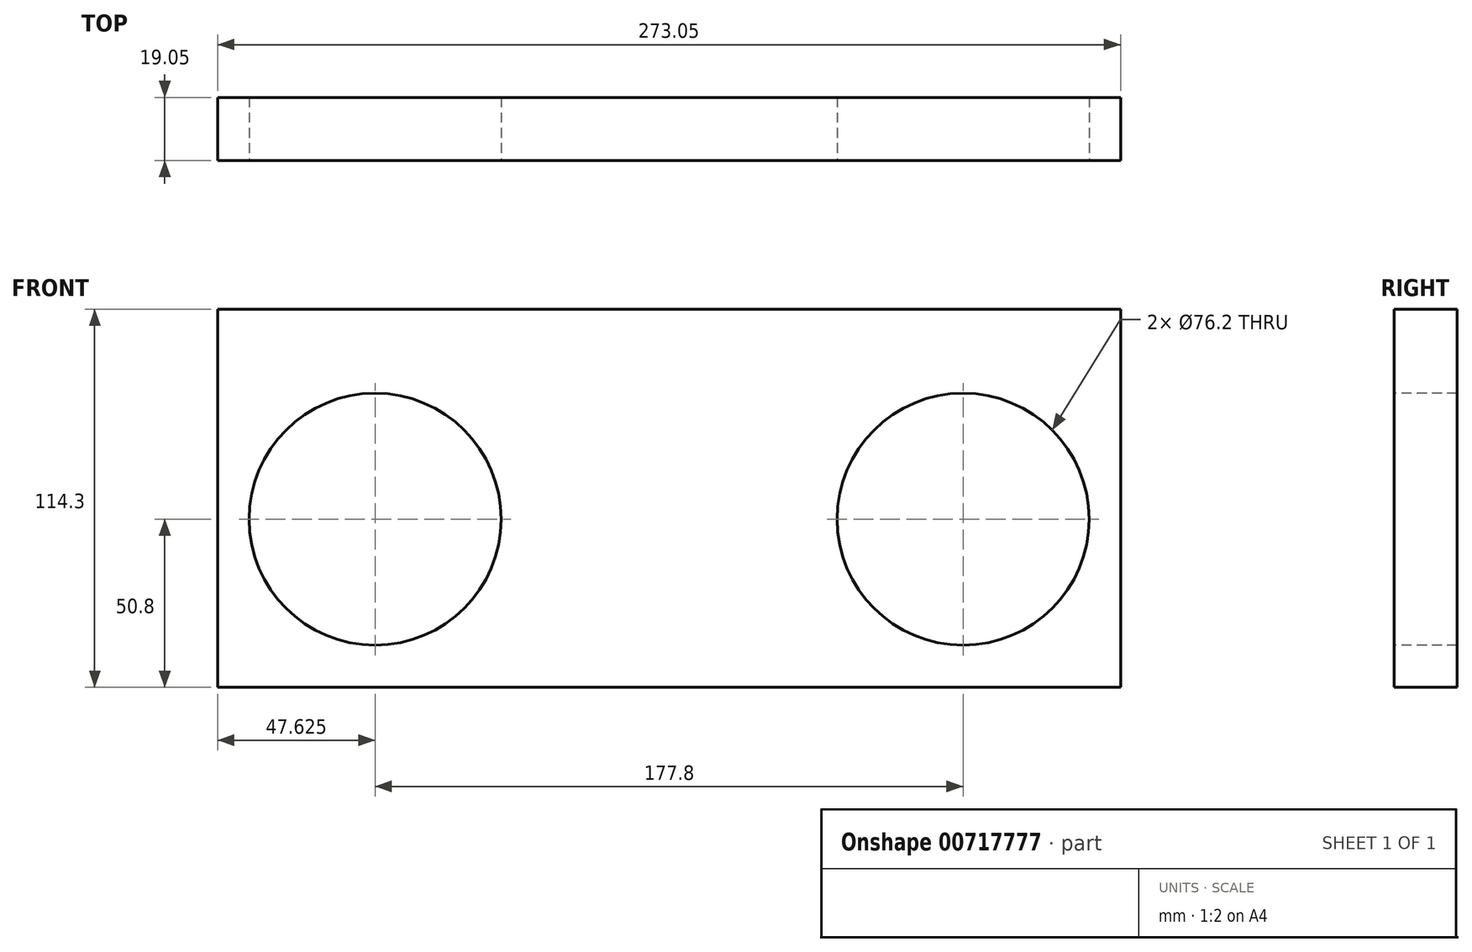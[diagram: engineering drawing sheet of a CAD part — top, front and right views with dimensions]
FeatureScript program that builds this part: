
annotation { "Feature Type Name" : "Feature", "Feature Type Description" : "" }
export const myFeature = defineFeature(function(context is Context, id is Id, definition is map)
    precondition{}
    {
        {
            var Q0;
            Q0=qCreatedBy(makeId("Front.planeOp"),FACE);
            var sketch = newSketch(context, id + "F0", { "sketchPlane" : qUnion([Q0])});
            skLineSegment(sketch, "E0.bottom", {"start": v(0, 0) * mm, "end": v(273.05, 0) * mm});
            skLineSegment(sketch, "E0.top", {"start": v(0, 114.3) * mm, "end": v(273.05, 114.3) * mm});
            skLineSegment(sketch, "E0.left", {"start": v(0, 0) * mm, "end": v(0, 114.3) * mm});
            skLineSegment(sketch, "E0.right", {"start": v(273.05, 0) * mm, "end": v(273.05, 114.3) * mm});
            skSolve(sketch);
        }
        {
            var Q0;
            Q0=makeQuery(id+"F0.imprint","IMPRINT",FACE,{"disambiguationData":[TD([[makeQuery(id+"F0.imprint","IMPRINT",EDGE,{"derivedFrom":sQuery(id+"F0.wireOp",EDGE,"E0.bottom")}),1.0]])]});
            extrude(context, id + "F1", {"entities" : qUnion([Q0]), "depth" : 19.05 * mm, "offsetDistance" : 25.4 * mm});
        }
        {
            var Q0;
            Q0=makeQuery(id+"F1.opExtrude","CAP_FACE",FACE,{"disambiguationData":[OSD([sQuery(id+"F0.wireOp",EDGE,"E0.bottom"),sQuery(id+"F0.wireOp",EDGE,"E0.top"),sQuery(id+"F0.wireOp",EDGE,"E0.left"),sQuery(id+"F0.wireOp",EDGE,"E0.right")])],"isStart":false});
            var sketch = newSketch(context, id + "F2", { "sketchPlane" : qUnion([Q0])});
            skCircle(sketch, "E1", {"center": v(47.63, 50.8) * mm, "radius": 38.1 * mm});
            skCircle(sketch, "E2", {"center": v(225.43, 50.8) * mm, "radius": 38.1 * mm});
            skSolve(sketch);
        }
        {
            var Q0;
            Q0=makeQuery(id+"F2.imprint","IMPRINT",FACE,{"disambiguationData":[TD([[makeQuery(id+"F2.imprint","IMPRINT",EDGE,{"derivedFrom":sQuery(id+"F2.wireOp",EDGE,"E1")}),1.0]])]});
            var Q1;
            Q1=makeQuery(id+"F2.imprint","IMPRINT",FACE,{"disambiguationData":[TD([[makeQuery(id+"F2.imprint","IMPRINT",EDGE,{"derivedFrom":sQuery(id+"F2.wireOp",EDGE,"E2")}),1.0]])]});
            extrude(context, id + "F3", {"entities" : qUnion([Q0, Q1]), "operationType" : NewBodyOperationType.REMOVE, "oppositeDirection" : true, "depth" : 25.4 * mm, "offsetDistance" : 25.4 * mm});
        }
    });
